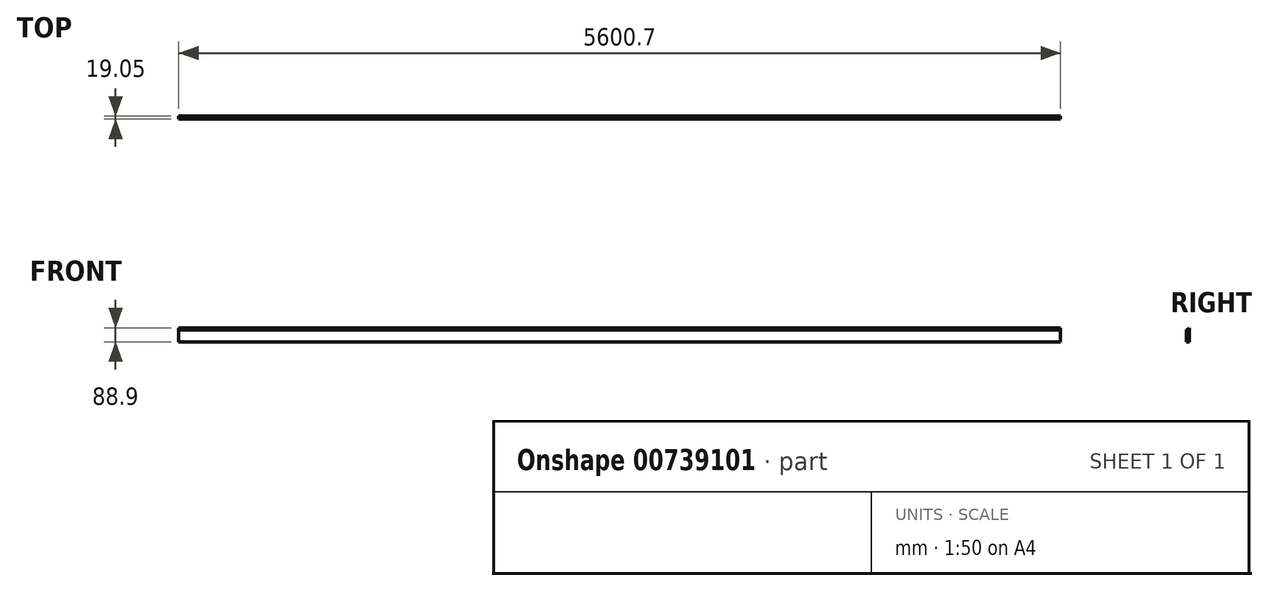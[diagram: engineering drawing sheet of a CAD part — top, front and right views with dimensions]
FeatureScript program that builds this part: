
annotation { "Feature Type Name" : "Feature", "Feature Type Description" : "" }
export const myFeature = defineFeature(function(context is Context, id is Id, definition is map)
    precondition{}
    {
        {
            var Q0;
            Q0=qCreatedBy(makeId("Right.planeOp"),FACE);
            var sketch = newSketch(context, id + "F0", { "sketchPlane" : qUnion([Q0])});
            skLineSegment(sketch, "E0", {"start": v(0, 0) * mm, "end": v(0, 75.56) * mm});
            skLineSegment(sketch, "E1", {"start": v(0, 75.56) * mm, "end": v(19.05, 88.9) * mm});
            skLineSegment(sketch, "E2", {"start": v(19.05, 88.9) * mm, "end": v(19.05, 0) * mm});
            skLineSegment(sketch, "E3", {"start": v(19.05, 0) * mm, "end": v(0, 0) * mm});
            skSolve(sketch);
        }
        {
            var Q0;
            Q0 = qSketchRegion(id + "F0", true);
            extrude(context, id + "F1", {"entities" : qUnion([Q0]), "depth" : 5600.7 * mm, "offsetDistance" : 25.4 * mm});
        }
    });
